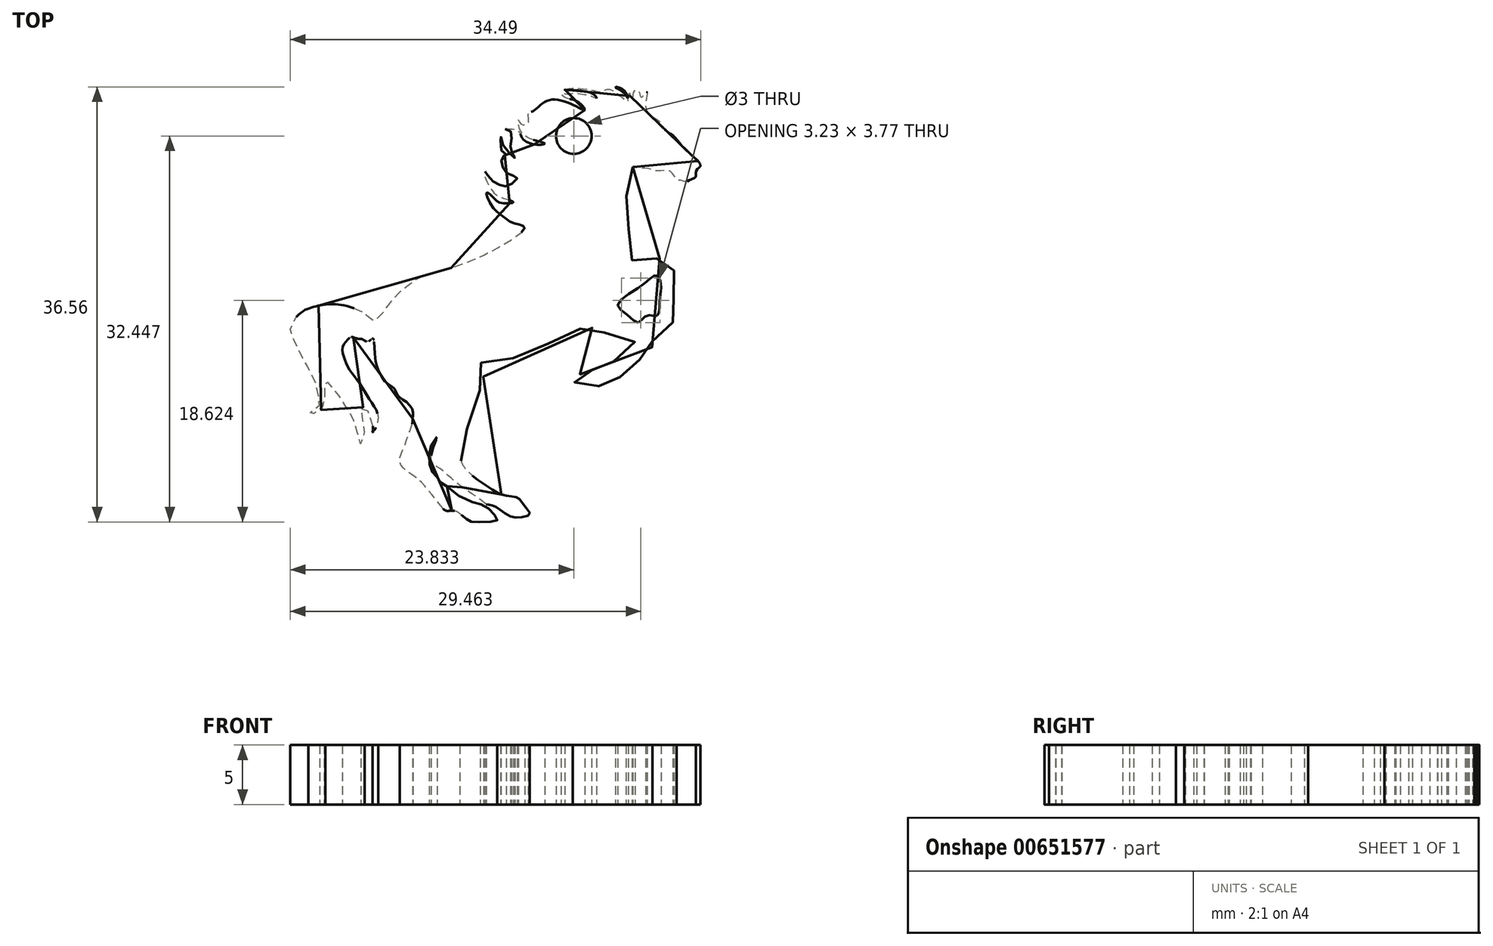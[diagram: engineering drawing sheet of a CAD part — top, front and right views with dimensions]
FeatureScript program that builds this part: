
annotation { "Feature Type Name" : "Feature", "Feature Type Description" : "" }
export const myFeature = defineFeature(function(context is Context, id is Id, definition is map)
    precondition{}
    {
        {
            var Q0;
            Q0=qCreatedBy(makeId("Top.planeOp"),FACE);
            var sketch = newSketch(context, id + "F0", { "sketchPlane" : qUnion([Q0])});
            skFitSpline(sketch, "E0", {"points": [v(40.65, 32.28) * mm, v(39.65, 33.03) * mm, v(38.92, 33.82) * mm, v(40.63, 35.2) * mm, v(41.75, 36.07) * mm, v(42.18, 36.28) * mm, v(42.57, 35.63) * mm, v(42.48, 34.4) * mm, v(42.43, 33.38) * mm, v(42.32, 32.96) * mm, v(42.01, 32.84) * mm, v(41.52, 32.91) * mm, v(41.03, 32.63) * mm, v(40.65, 32.28) * mm]});
            skFitSpline(sketch, "E1", {"points": [v(40.2, 45.37) * mm, v(39.92, 44.59) * mm, v(39.77, 43.72) * mm, v(39.65, 42.58) * mm, v(39.73, 41.2) * mm, v(39.84, 40.3) * mm, v(39.96, 39.55) * mm, v(40.2, 38.52) * mm, v(40.2, 37.46) * mm, v(41.06, 37.5) * mm, v(41.7, 37.62) * mm, v(42.18, 37.7) * mm, v(42.87, 37.58) * mm, v(43.5, 37.3) * mm, v(43.62, 36.99) * mm, v(43.66, 36.28) * mm, v(43.62, 35.57) * mm, v(43.58, 34.63) * mm, v(43.74, 33.84) * mm, v(43.82, 33.1) * mm, v(43.86, 32.54) * mm, v(43.23, 32.1) * mm, v(42.6, 31.4) * mm, v(41.85, 30.93) * mm, v(41.85, 30.34) * mm, v(41.62, 29.9) * mm, v(41.3, 29.63) * mm, v(40.7, 29.16) * mm, v(40, 28.65) * mm, v(39.6, 28.17) * mm, v(39.14, 27.74) * mm, v(38.82, 27.35) * mm, v(38.15, 27.3) * mm, v(37.52, 27.07) * mm, v(36.85, 26.72) * mm, v(35.24, 26.72) * mm, v(35.28, 27.23) * mm, v(35.75, 27.94) * mm, v(36.1, 28.21) * mm, v(36.42, 28.33) * mm, v(37.05, 28.25) * mm, v(37.4, 28.1) * mm, v(37.76, 28.45) * mm, v(38.58, 29.04) * mm, v(39.53, 29.55) * mm, v(40.32, 30.38) * mm, v(40.36, 30.7) * mm, v(39.96, 30.81) * mm, v(38.39, 31.24) * mm, v(37.52, 31.56) * mm, v(36.73, 31.87) * mm, v(36.3, 32) * mm, v(35.67, 31.72) * mm, v(34.41, 31.13) * mm, v(33.27, 30.61) * mm, v(32.29, 30.14) * mm, v(30.6, 29.43) * mm, v(29.41, 29.16) * mm, v(28.23, 28.96) * mm, v(27.4, 28.88) * mm, v(27.56, 28.3) * mm, v(27.6, 27.46) * mm, v(27.2, 26.24) * mm, v(26.74, 24.51) * mm, v(26.1, 23.02) * mm, v(25.67, 21.68) * mm, v(25.71, 20.81) * mm, v(26.07, 20.1) * mm, v(27.1, 19.12) * mm, v(27.8, 18.65) * mm, v(28.78, 18.02) * mm, v(29.37, 17.78) * mm, v(30.16, 17.66) * mm, v(30.63, 17.5) * mm, v(31.1, 16.88) * mm, v(31.54, 16.2) * mm, v(30.71, 15.93) * mm, v(29.8, 16.05) * mm, v(28.9, 16.68) * mm, v(28.47, 16.92) * mm, v(28.08, 17) * mm, v(27.92, 17) * mm, v(27.33, 17.47) * mm, v(26.38, 18.1) * mm, v(25.08, 19.08) * mm, v(23.98, 20.03) * mm, v(23.31, 20.58) * mm, v(23.31, 21.44) * mm, v(23.55, 22.2) * mm, v(23.75, 22.7) * mm, v(23.27, 22) * mm, v(23.08, 20.81) * mm, v(23.27, 19.83) * mm, v(23.7, 19.36) * mm, v(24.02, 18.88) * mm, v(24.77, 18.41) * mm, v(25.4, 17.86) * mm, v(25.83, 17.63) * mm, v(26.46, 17.31) * mm, v(27.45, 17) * mm, v(28.27, 16.48) * mm, v(28.78, 15.81) * mm, v(28.78, 15.66) * mm, v(27.52, 15.54) * mm, v(26.58, 15.58) * mm, v(26.27, 15.74) * mm, v(25.83, 16.1) * mm, v(25.4, 16.4) * mm, v(24.89, 16.48) * mm, v(24.5, 16.48) * mm, v(23.98, 17) * mm, v(23.35, 17.78) * mm, v(22.45, 18.85) * mm, v(21.82, 19.4) * mm, v(20.95, 20.03) * mm, v(20.6, 20.66) * mm, v(20.8, 21.4) * mm, v(21.23, 22.54) * mm, v(21.54, 23.41) * mm, v(21.7, 23.92) * mm, v(21.7, 24.32) * mm, v(21.7, 24.9) * mm, v(21.07, 25.7) * mm, v(20.44, 26.17) * mm, v(20.16, 26.76) * mm, v(19.42, 27.3) * mm, v(18.63, 28.84) * mm, v(18.51, 29.75) * mm, v(18.35, 30.97) * mm, v(18.12, 30.81) * mm, v(17.72, 30.73) * mm, v(17.49, 30.89) * mm, v(16.94, 30.97) * mm, v(16.58, 31.09) * mm, v(16.15, 30.77) * mm, v(15.8, 30.18) * mm, v(15.95, 29.28) * mm, v(16.43, 28.3) * mm, v(17.33, 27.03) * mm, v(18.24, 25.58) * mm, v(18.79, 24.24) * mm, v(18.35, 23.06) * mm, v(18.31, 24.12) * mm, v(17.45, 25.18) * mm, v(17.37, 24.47) * mm, v(17.65, 23.33) * mm, v(17.3, 22.11) * mm, v(16.98, 23.53) * mm, v(16.43, 24.63) * mm, v(15.4, 26.32) * mm, v(14.3, 27.39) * mm, v(14.34, 26.56) * mm, v(14.22, 25.73) * mm, v(13.83, 24.79) * mm, v(12.92, 24.63) * mm, v(13.75, 25.14) * mm, v(13.83, 25.81) * mm, v(13.63, 27) * mm, v(12.37, 29.47) * mm, v(11.7, 30.85) * mm, v(11.43, 31.91) * mm, v(12.41, 33.21) * mm, v(13.36, 33.6) * mm, v(14.5, 33.84) * mm, v(15.8, 33.76) * mm, v(17.76, 33.01) * mm, v(18.43, 32.5) * mm, v(19.46, 33.49) * mm, v(20.52, 34.79) * mm, v(21.54, 35.61) * mm, v(22.68, 36.28) * mm, v(24.34, 36.71) * mm, v(25.64, 37.15) * mm, v(27.68, 37.97) * mm, v(31.1, 40.3) * mm, v(30.08, 40.69) * mm, v(29.34, 41.2) * mm, v(28.4, 42.03) * mm, v(27.92, 43.25) * mm, v(28.63, 42.66) * mm, v(29.18, 42.34) * mm, v(30.16, 42.38) * mm, v(29.73, 42.62) * mm, v(28.7, 43.05) * mm, v(27.76, 44.7) * mm, v(27.8, 44.98) * mm, v(28.2, 44.39) * mm, v(29.1, 43.84) * mm, v(29.8, 43.84) * mm, v(30.48, 44.47) * mm, v(29.77, 44.74) * mm, v(29.26, 45.41) * mm, v(29.22, 46.2) * mm, v(29.57, 46.44) * mm, v(29.26, 46.6) * mm, v(29.1, 47.93) * mm, v(29.3, 47.22) * mm, v(30.28, 46.16) * mm, v(29.96, 46.67) * mm, v(30, 47.85) * mm, v(29.77, 48.52) * mm, v(29.1, 48.56) * mm, v(30.44, 48.48) * mm, v(30.9, 47.81) * mm, v(32.05, 47.26) * mm, v(32.8, 47.34) * mm, v(31.74, 47.7) * mm, v(30.67, 48.6) * mm, v(30.6, 49.35) * mm, v(30.8, 49) * mm, v(31.42, 49.11) * mm, v(31.4, 49.78) * mm, v(31.87, 50.11) * mm, v(33.06, 50.97) * mm, v(35.24, 50.58) * mm, v(36.17, 50.18) * mm, v(35.5, 50.9) * mm, v(34.45, 51.24) * mm, v(34.18, 51.57) * mm, v(34.67, 51.51) * mm, v(35.25, 51.58) * mm, v(35.84, 51.52) * mm, v(36.3, 51.46) * mm, v(36.68, 51.35) * mm, v(37.15, 51.16) * mm, v(36.93, 51.47) * mm, v(36.35, 51.7) * mm, v(35.65, 51.8) * mm, v(34.9, 51.84) * mm, v(34.47, 51.87) * mm, v(34.87, 51.98) * mm, v(36, 51.96) * mm, v(37, 51.79) * mm, v(37.47, 51.67) * mm, v(37.86, 51.85) * mm, v(38.57, 51.77) * mm, v(39.78, 50.9) * mm, v(39.54, 51.51) * mm, v(38.75, 52.09) * mm, v(39.54, 51.75) * mm, v(39.8, 51.17) * mm, v(39.9, 51.62) * mm, v(40.04, 51.1) * mm, v(40.2, 51.2) * mm, v(40.25, 51.62) * mm, v(40.54, 51.88) * mm, v(40.78, 51.56) * mm, v(40.9, 51.22) * mm, v(41.3, 51.64) * mm, v(41.4, 51.64) * mm, v(41.35, 50.12) * mm, v(42.46, 49.2) * mm, v(42.85, 48.57) * mm, v(43.7, 47.91) * mm, v(44.45, 47.02) * mm, v(45.9, 45.52) * mm, v(45.66, 45.23) * mm, v(45.5, 44.87) * mm, v(45.48, 44.55) * mm, v(44.93, 44.26) * mm, v(44.61, 44.13) * mm, v(44.24, 44.26) * mm, v(44, 44.26) * mm, v(43.48, 44.9) * mm, v(43.06, 45.08) * mm, v(42.18, 45.05) * mm, v(41.6, 45.2) * mm, v(40.88, 45.29) * mm, v(40.6, 45.3) * mm, v(40.46, 45.37) * mm, v(40.31, 45.42) * mm, v(40.26, 45.45) * mm, v(40.2, 45.37) * mm]});
            skCircle(sketch, "E2", {"center": v(35.24, 47.99) * mm, "radius": 1.5 * mm});
            skSolve(sketch);
        }
        {
            var Q0;
            Q0=makeQuery(id+"F0.imprint","IMPRINT",FACE,{"disambiguationData":[TD([[makeQuery(id+"F0.imprint","IMPRINT",EDGE,{"derivedFrom":sQuery(id+"F0.wireOp",EDGE,"E0")}),1.0]])]});
            extrude(context, id + "F1", {"entities" : qUnion([Q0]), "depth" : 5 * mm, "offsetDistance" : 25 * mm});
        }
    });
